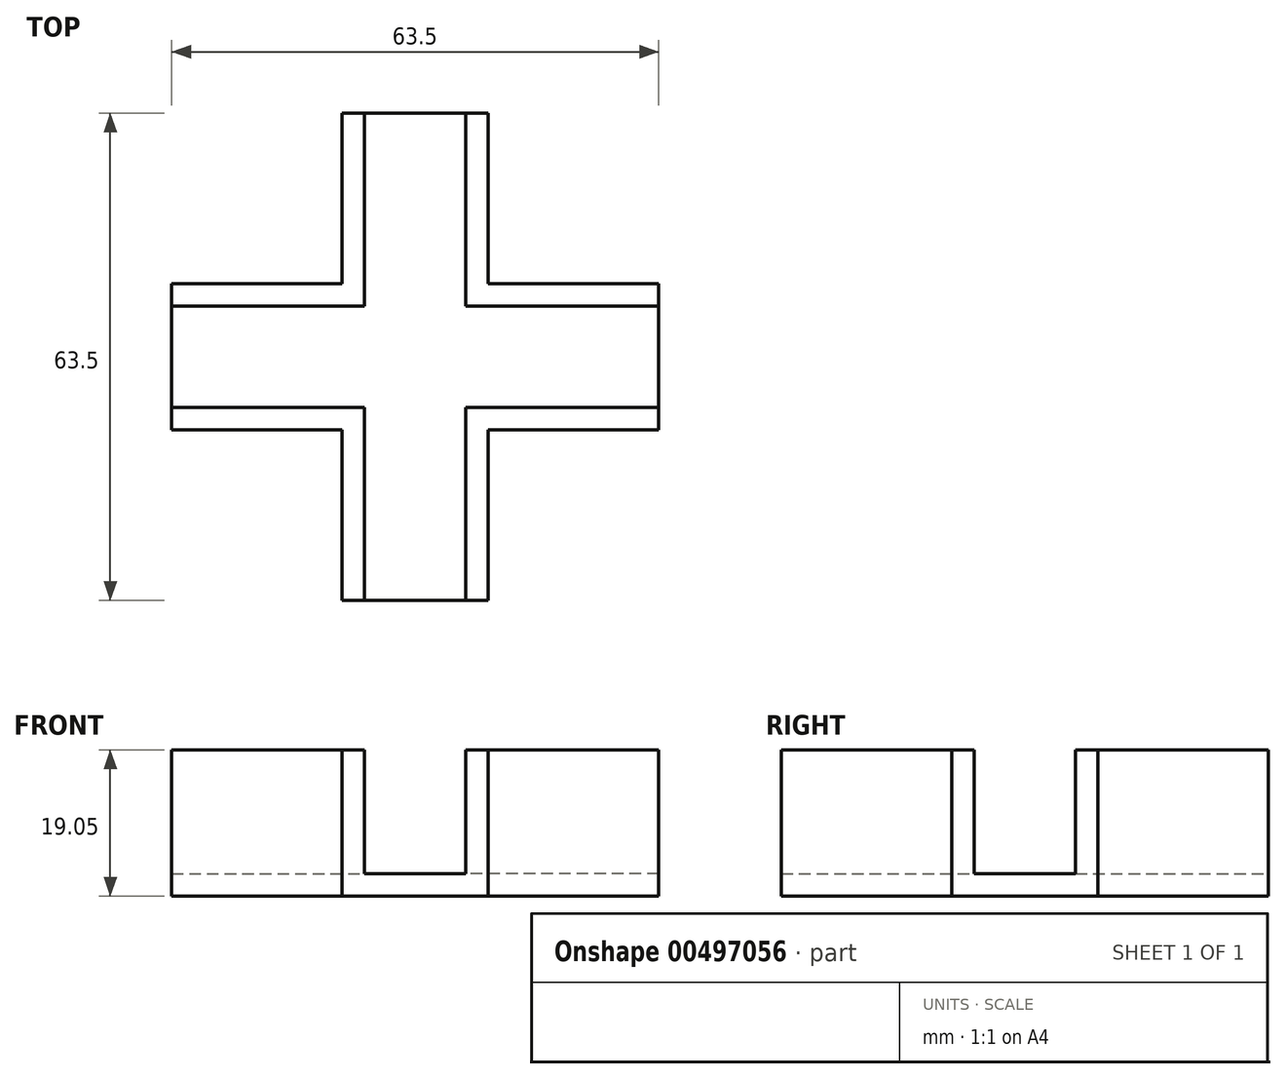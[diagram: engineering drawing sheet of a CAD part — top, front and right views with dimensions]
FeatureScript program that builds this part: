
annotation { "Feature Type Name" : "Feature", "Feature Type Description" : "" }
export const myFeature = defineFeature(function(context is Context, id is Id, definition is map)
    precondition{}
    {
        {
            var Q0;
            Q0=qCreatedBy(makeId("Top.planeOp"),FACE);
            var sketch = newSketch(context, id + "F0", { "sketchPlane" : qUnion([Q0])});
            skLineSegment(sketch, "E0", {"start": v(-9.93, 32) * mm, "end": v(9.12, 32) * mm});
            skLineSegment(sketch, "E1", {"start": v(9.12, 32) * mm, "end": v(9.12, 9.77) * mm});
            skLineSegment(sketch, "E2", {"start": v(9.12, 9.77) * mm, "end": v(31.34, 9.77) * mm});
            skLineSegment(sketch, "E3", {"start": v(31.34, 9.77) * mm, "end": v(31.34, -9.28) * mm});
            skLineSegment(sketch, "E4", {"start": v(31.34, -9.28) * mm, "end": v(9.12, -9.28) * mm});
            skLineSegment(sketch, "E5", {"start": v(9.12, -9.28) * mm, "end": v(9.12, -31.5) * mm});
            skLineSegment(sketch, "E6", {"start": v(9.12, -31.5) * mm, "end": v(-9.93, -31.5) * mm});
            skLineSegment(sketch, "E7", {"start": v(-9.93, -31.5) * mm, "end": v(-9.93, -9.28) * mm});
            skLineSegment(sketch, "E8", {"start": v(-9.93, -9.28) * mm, "end": v(-32.16, -9.28) * mm});
            skLineSegment(sketch, "E9", {"start": v(-32.16, -9.28) * mm, "end": v(-32.16, 9.77) * mm});
            skLineSegment(sketch, "E10", {"start": v(-32.16, 9.77) * mm, "end": v(-9.93, 9.77) * mm});
            skLineSegment(sketch, "E11", {"start": v(-9.93, 9.77) * mm, "end": v(-9.93, 32) * mm});
            skSolve(sketch);
        }
        {
            var Q0;
            Q0=makeQuery(id+"F0.imprint","IMPRINT",FACE,{"disambiguationData":[TD([[makeQuery(id+"F0.imprint","IMPRINT",EDGE,{"derivedFrom":sQuery(id+"F0.wireOp",EDGE,"E0")}),-1.0]])]});
            extrude(context, id + "F1", {"entities" : qUnion([Q0]), "depth" : 19.05 * mm, "offsetDistance" : 25.4 * mm});
        }
        {
            var Q0;
            Q0=makeQuery(id+"F1.opExtrude","CAP_FACE",FACE,{"disambiguationData":[OSD([sQuery(id+"F0.wireOp",EDGE,"E0"),sQuery(id+"F0.wireOp",EDGE,"E1"),sQuery(id+"F0.wireOp",EDGE,"E2"),sQuery(id+"F0.wireOp",EDGE,"E3"),sQuery(id+"F0.wireOp",EDGE,"E4"),sQuery(id+"F0.wireOp",EDGE,"E5"),sQuery(id+"F0.wireOp",EDGE,"E6"),sQuery(id+"F0.wireOp",EDGE,"E7"),sQuery(id+"F0.wireOp",EDGE,"E8"),sQuery(id+"F0.wireOp",EDGE,"E9"),sQuery(id+"F0.wireOp",EDGE,"E10"),sQuery(id+"F0.wireOp",EDGE,"E11")])],"isStart":false});
            var Q1;
            Q1=makeQuery(id+"F1.opExtrude","SWEPT_FACE",FACE,{"disambiguationData":[OSD([sQuery(id+"F0.wireOp",EDGE,"E6")])]});
            var Q2;
            Q2=makeQuery(id+"F1.opExtrude","SWEPT_FACE",FACE,{"disambiguationData":[OSD([sQuery(id+"F0.wireOp",EDGE,"E3")])]});
            var Q3;
            Q3=makeQuery(id+"F1.opExtrude","SWEPT_FACE",FACE,{"disambiguationData":[OSD([sQuery(id+"F0.wireOp",EDGE,"E0")])]});
            var Q4;
            Q4=makeQuery(id+"F1.opExtrude","SWEPT_FACE",FACE,{"disambiguationData":[OSD([sQuery(id+"F0.wireOp",EDGE,"E9")])]});
            shell(context, id + "F2", {"entities" : qUnion([Q0, Q1, Q2, Q3, Q4]), "thickness" : 2.92 * mm});
        }
    });
